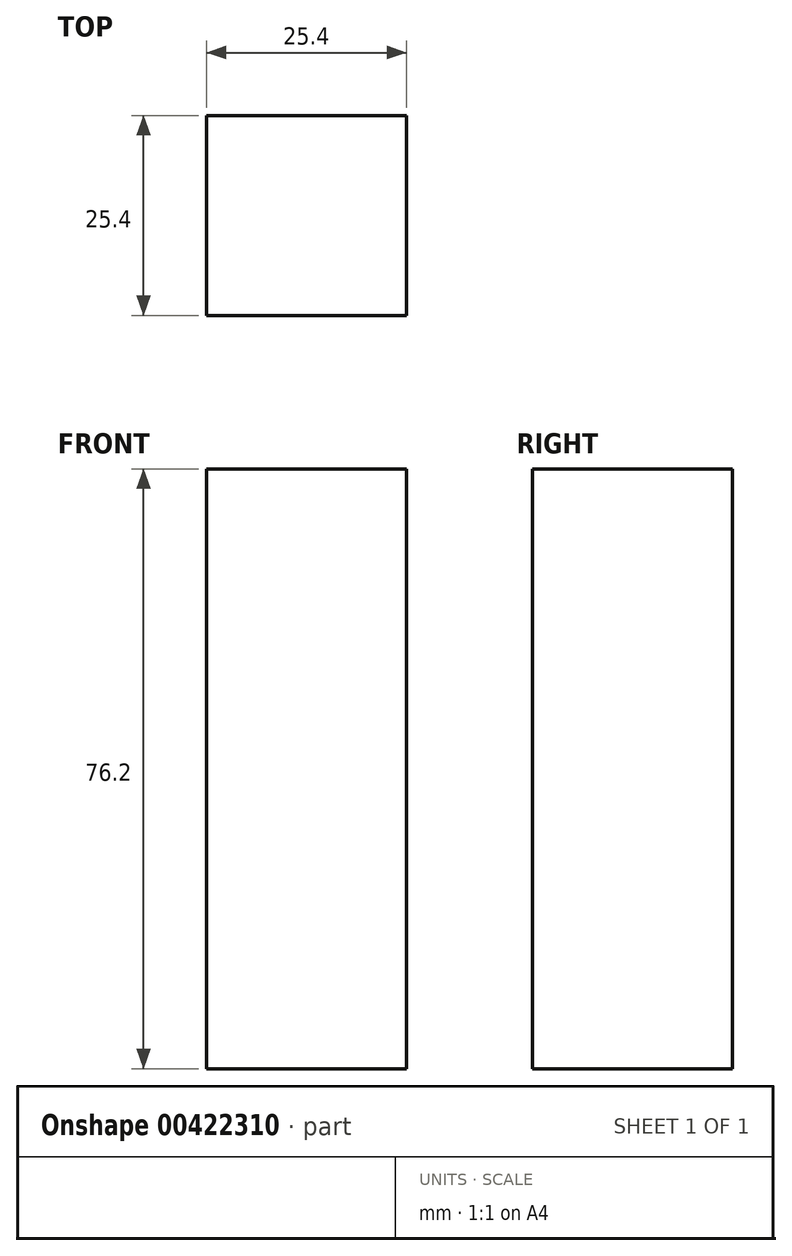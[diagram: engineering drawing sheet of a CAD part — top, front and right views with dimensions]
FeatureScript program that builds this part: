
annotation { "Feature Type Name" : "Feature", "Feature Type Description" : "" }
export const myFeature = defineFeature(function(context is Context, id is Id, definition is map)
    precondition{}
    {
        {
            var Q0;
            Q0=qCreatedBy(makeId("Front.planeOp"),FACE);
            var sketch = newSketch(context, id + "F0", { "sketchPlane" : qUnion([Q0])});
            skLineSegment(sketch, "E0.bottom", {"start": v(-49.65, -35.9) * mm, "end": v(-24.25, -35.9) * mm});
            skLineSegment(sketch, "E0.top", {"start": v(-49.65, 40.3) * mm, "end": v(-24.25, 40.3) * mm});
            skLineSegment(sketch, "E0.left", {"start": v(-49.65, -35.9) * mm, "end": v(-49.65, 40.3) * mm});
            skLineSegment(sketch, "E0.right", {"start": v(-24.25, -35.9) * mm, "end": v(-24.25, 40.3) * mm});
            skSolve(sketch);
        }
        {
            var Q0;
            Q0 = qSketchRegion(id + "F0", true);
            extrude(context, id + "F1", {"entities" : qUnion([Q0]), "depth" : 25.4 * mm});
        }
    });
